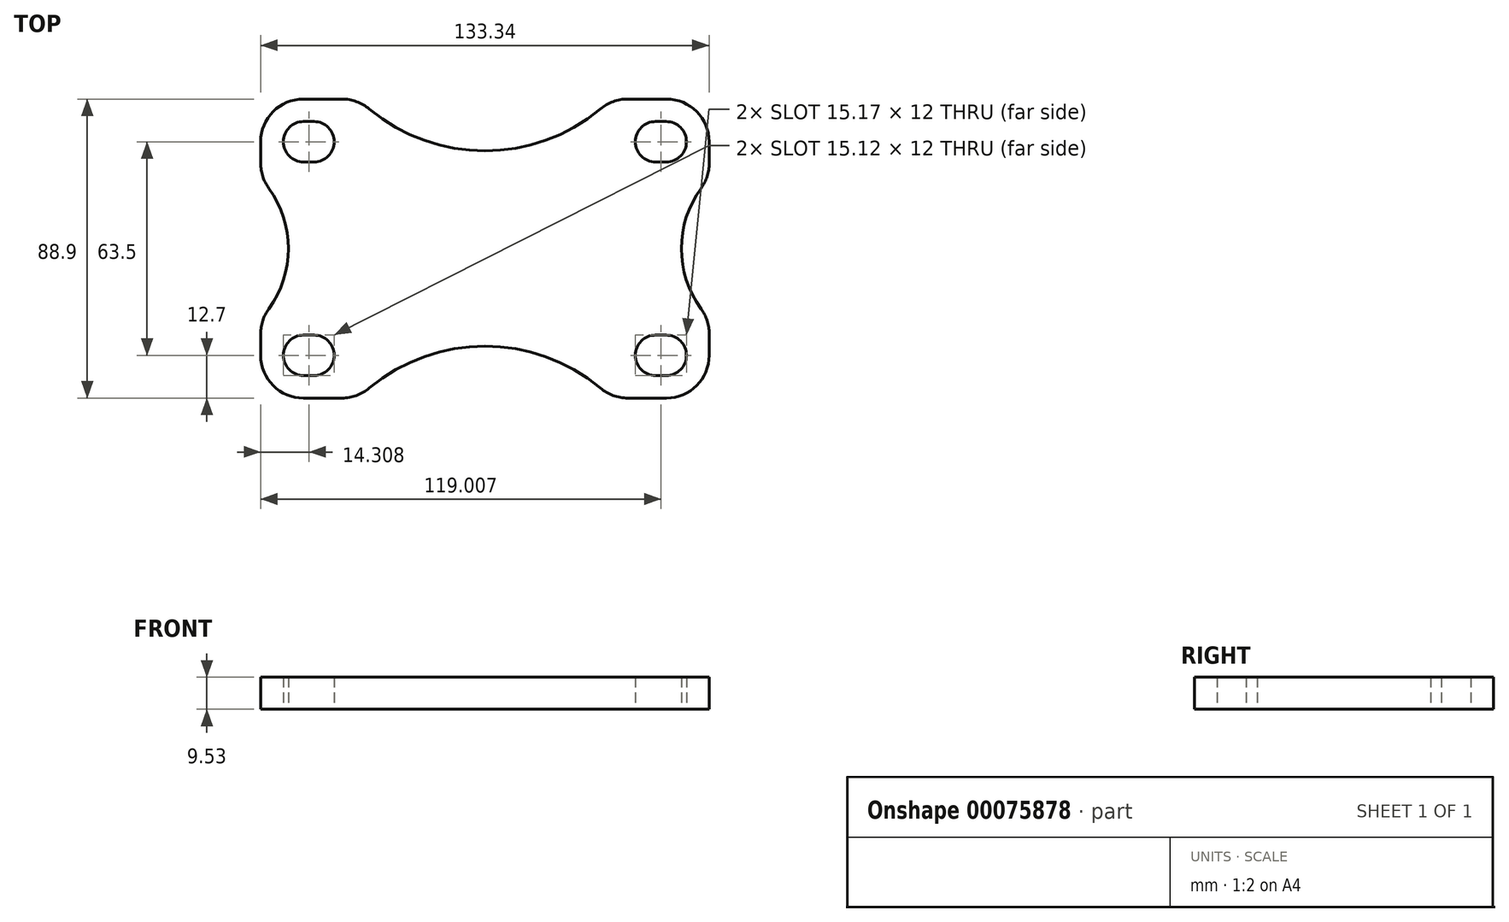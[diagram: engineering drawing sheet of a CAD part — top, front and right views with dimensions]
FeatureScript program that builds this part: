
annotation { "Feature Type Name" : "Feature", "Feature Type Description" : "" }
export const myFeature = defineFeature(function(context is Context, id is Id, definition is map)
    precondition{}
    {
        {
            var Q0;
            Q0=qCreatedBy(makeId("Top.planeOp"),FACE);
            var sketch = newSketch(context, id + "F0", { "sketchPlane" : qUnion([Q0])});
            skLineSegment(sketch, "E0.bottom", {"start": v(53.97, 44.45) * mm, "end": v(42.48, 44.45) * mm});
            skLineSegment(sketch, "E0.top", {"start": v(53.98, -44.45) * mm, "end": v(42.48, -44.45) * mm});
            skLineSegment(sketch, "E0.left", {"start": v(66.67, 31.75) * mm, "end": v(66.68, 25.36) * mm});
            skLineSegment(sketch, "E0.right", {"start": v(-66.68, 31.75) * mm, "end": v(-66.68, 25.36) * mm});
            skPoint(sketch, "E0.middle", {"position": v(0, 0) * mm});
            skPoint(sketch, "E1.visualSharp", {"position": v(66.68, 44.45) * mm});
            skArc(sketch, "E1.filletArc", {"start": v(66.67, 31.75) * mm, "mid": v(62.96, 40.73) * mm, "end": v(53.97, 44.45) * mm});
            skPoint(sketch, "E2.visualSharp", {"position": v(66.68, -44.45) * mm});
            skArc(sketch, "E2.filletArc", {"start": v(53.98, -44.45) * mm, "mid": v(62.96, -40.73) * mm, "end": v(66.68, -31.75) * mm});
            skPoint(sketch, "E3.visualSharp", {"position": v(-66.67, -44.45) * mm});
            skArc(sketch, "E3.filletArc", {"start": v(-66.67, -31.75) * mm, "mid": v(-62.96, -40.73) * mm, "end": v(-53.98, -44.45) * mm});
            skPoint(sketch, "E4.visualSharp", {"position": v(-66.68, 44.45) * mm});
            skArc(sketch, "E4.filletArc", {"start": v(-53.98, 44.45) * mm, "mid": v(-62.96, 40.73) * mm, "end": v(-66.67, 31.75) * mm});
            skArc(sketch, "E5", {"start": v(53.92, 25.75) * mm, "mid": v(59.93, 31.75) * mm, "end": v(53.92, 37.75) * mm});
            skArc(sketch, "E6", {"start": v(-53.92, 37.75) * mm, "mid": v(-59.93, 31.75) * mm, "end": v(-53.92, 25.75) * mm});
            skArc(sketch, "E7", {"start": v(53.93, -37.75) * mm, "mid": v(59.93, -31.75) * mm, "end": v(53.93, -25.75) * mm});
            skArc(sketch, "E8", {"start": v(-53.93, -25.75) * mm, "mid": v(-59.93, -31.75) * mm, "end": v(-53.93, -37.75) * mm});
            skArc(sketch, "E9", {"start": v(-50.8, 25.75) * mm, "mid": v(-44.8, 31.75) * mm, "end": v(-50.8, 37.75) * mm});
            skArc(sketch, "E10", {"start": v(-50.8, -37.75) * mm, "mid": v(-44.8, -31.75) * mm, "end": v(-50.8, -25.75) * mm});
            skArc(sketch, "E11", {"start": v(50.75, -25.75) * mm, "mid": v(44.75, -31.75) * mm, "end": v(50.75, -37.75) * mm});
            skArc(sketch, "E12", {"start": v(50.75, 37.75) * mm, "mid": v(44.75, 31.75) * mm, "end": v(50.75, 25.75) * mm});
            skLineSegment(sketch, "E13", {"start": v(-53.92, 37.75) * mm, "end": v(-50.8, 37.75) * mm});
            skLineSegment(sketch, "E14", {"start": v(-53.92, 25.75) * mm, "end": v(-50.8, 25.75) * mm});
            skLineSegment(sketch, "E15", {"start": v(-53.93, -25.75) * mm, "end": v(-50.8, -25.75) * mm});
            skLineSegment(sketch, "E16", {"start": v(-53.93, -37.75) * mm, "end": v(-50.8, -37.75) * mm});
            skLineSegment(sketch, "E17", {"start": v(50.75, 37.75) * mm, "end": v(53.92, 37.75) * mm});
            skLineSegment(sketch, "E18", {"start": v(53.92, 25.75) * mm, "end": v(50.75, 25.75) * mm});
            skLineSegment(sketch, "E19.trimOffspring", {"start": v(50.75, -25.75) * mm, "end": v(53.93, -25.75) * mm});
            skLineSegment(sketch, "E20.trimOffspring", {"start": v(50.75, -37.75) * mm, "end": v(53.93, -37.75) * mm});
            skArc(sketch, "E21", {"start": v(-64.25, -17.9) * mm, "mid": v(-58.44, 0) * mm, "end": v(-64.25, 17.9) * mm});
            skArc(sketch, "E22", {"start": v(-34.33, 41.5) * mm, "mid": v(0, 29.03) * mm, "end": v(34.33, 41.5) * mm});
            skLineSegment(sketch, "E23.trimOffspring", {"start": v(-66.68, -25.36) * mm, "end": v(-66.68, -31.75) * mm});
            skLineSegment(sketch, "E24.trimOffspring", {"start": v(-42.48, 44.45) * mm, "end": v(-53.98, 44.45) * mm});
            skPoint(sketch, "E25.visualSharp", {"position": v(-37.59, 44.45) * mm});
            skArc(sketch, "E25.filletArc", {"start": v(-34.33, 41.5) * mm, "mid": v(-38.15, 43.69) * mm, "end": v(-42.48, 44.45) * mm});
            skPoint(sketch, "E26.visualSharp", {"position": v(37.59, 44.45) * mm});
            skArc(sketch, "E26.filletArc", {"start": v(42.48, 44.45) * mm, "mid": v(38.15, 43.69) * mm, "end": v(34.33, 41.5) * mm});
            skPoint(sketch, "E27.visualSharp", {"position": v(-66.68, 20.83) * mm});
            skArc(sketch, "E27.filletArc", {"start": v(-66.68, 25.36) * mm, "mid": v(-66.05, 21.43) * mm, "end": v(-64.25, 17.9) * mm});
            skPoint(sketch, "E28.visualSharp", {"position": v(-66.68, -20.83) * mm});
            skArc(sketch, "E28.filletArc", {"start": v(-64.25, -17.9) * mm, "mid": v(-66.05, -21.43) * mm, "end": v(-66.68, -25.36) * mm});
            skArc(sketch, "E29.MirrorCS", {"start": v(42.48, -44.45) * mm, "mid": v(38.15, -43.69) * mm, "end": v(34.33, -41.5) * mm});
            skArc(sketch, "E30.MirrorCS", {"start": v(-34.33, -41.5) * mm, "mid": v(0, -29.03) * mm, "end": v(34.33, -41.5) * mm});
            skArc(sketch, "E31.MirrorCS", {"start": v(-34.33, -41.5) * mm, "mid": v(-38.15, -43.69) * mm, "end": v(-42.48, -44.45) * mm});
            skArc(sketch, "E32.MirrorCS", {"start": v(-66.68, -25.36) * mm, "mid": v(-66.05, -21.43) * mm, "end": v(-64.25, -17.9) * mm});
            skArc(sketch, "E33.MirrorCS", {"start": v(-64.25, 17.9) * mm, "mid": v(-58.44, 0) * mm, "end": v(-64.25, -17.9) * mm});
            skArc(sketch, "E34.MirrorCS", {"start": v(-64.25, 17.9) * mm, "mid": v(-66.05, 21.43) * mm, "end": v(-66.68, 25.36) * mm});
            skArc(sketch, "E35.MirrorCS", {"start": v(64.25, -17.9) * mm, "mid": v(66.05, -21.43) * mm, "end": v(66.68, -25.36) * mm});
            skArc(sketch, "E36.MirrorCS", {"start": v(64.25, 17.9) * mm, "mid": v(66.05, 21.43) * mm, "end": v(66.68, 25.36) * mm});
            skArc(sketch, "E37.MirrorCS", {"start": v(64.25, -17.9) * mm, "mid": v(58.44, 0) * mm, "end": v(64.25, 17.9) * mm});
            skLineSegment(sketch, "E38.trimOffspring", {"start": v(66.68, -25.36) * mm, "end": v(66.68, -31.75) * mm});
            skLineSegment(sketch, "E39.trimOffspring", {"start": v(-42.48, -44.45) * mm, "end": v(-53.98, -44.45) * mm});
            skSolve(sketch);
        }
        {
            var Q0;
            Q0 = qSketchRegion(id + "F0", true);
            extrude(context, id + "F1", {"entities" : qUnion([Q0]), "depth" : 9.52 * mm});
        }
    });
